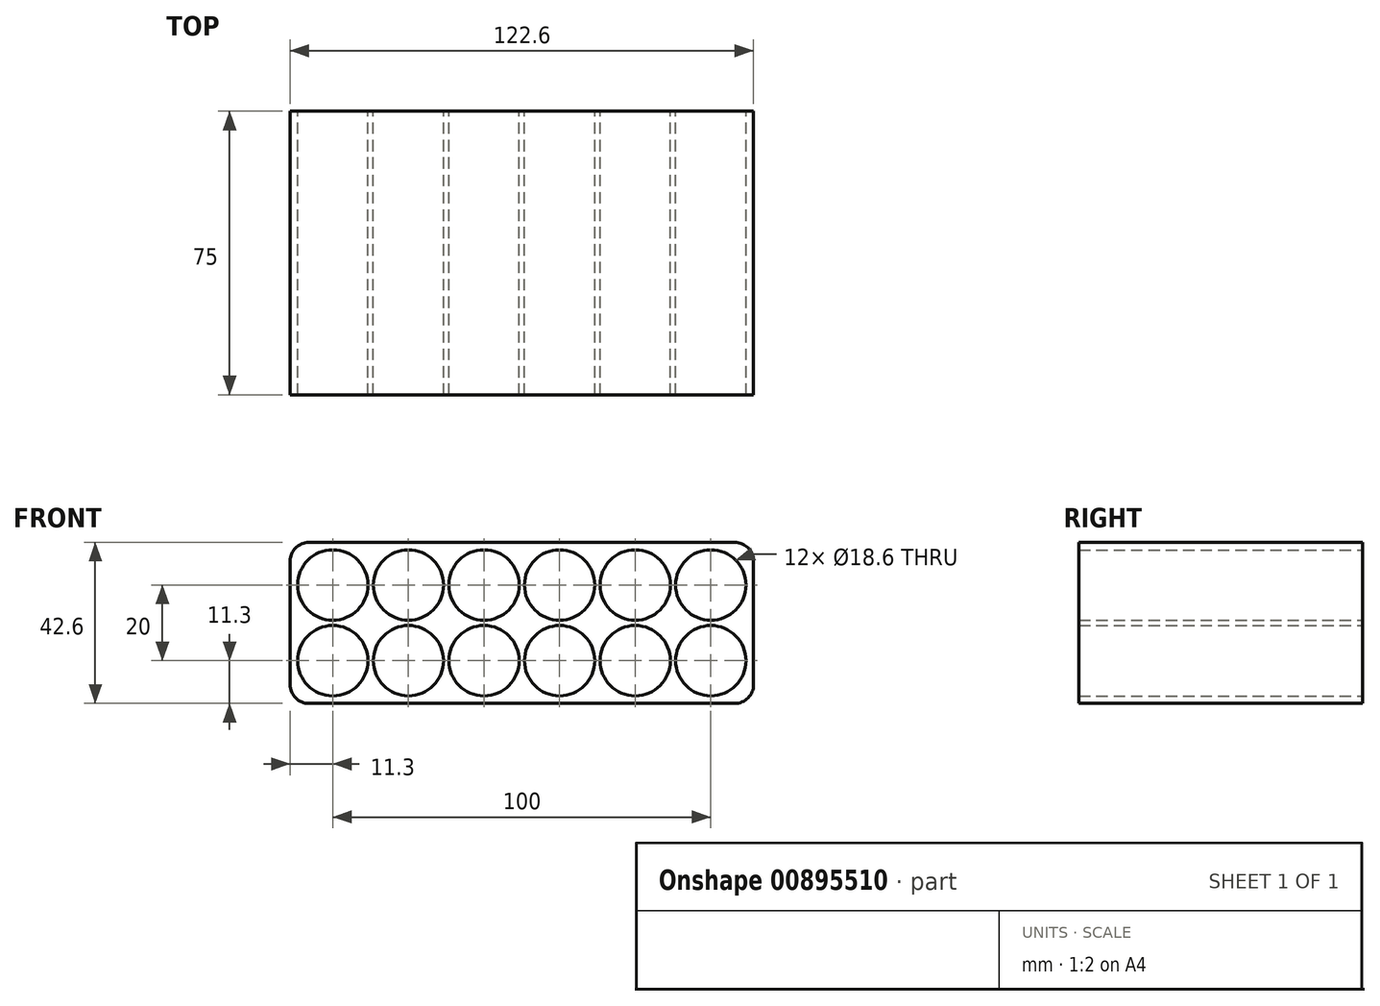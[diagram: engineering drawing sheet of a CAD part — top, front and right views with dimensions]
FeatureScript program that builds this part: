
annotation { "Feature Type Name" : "Feature", "Feature Type Description" : "" }
export const myFeature = defineFeature(function(context is Context, id is Id, definition is map)
    precondition{}
    {
        {
            var Q0;
            Q0=qCreatedBy(makeId("Front.planeOp"),FACE);
            var sketch = newSketch(context, id + "F0", { "sketchPlane" : qUnion([Q0])});
            skCircle(sketch, "E0", {"center": v(0, 0) * mm, "radius": 9.3 * mm});
            skCircle(sketch, "E1.0.1.0", {"center": v(0, 20) * mm, "radius": 9.3 * mm});
            skCircle(sketch, "E1.1.0.0", {"center": v(20, 0) * mm, "radius": 9.3 * mm});
            skCircle(sketch, "E1.1.1.0", {"center": v(20, 20) * mm, "radius": 9.3 * mm});
            skCircle(sketch, "E1.2.0.0", {"center": v(40, 0) * mm, "radius": 9.3 * mm});
            skCircle(sketch, "E1.2.1.0", {"center": v(40, 20) * mm, "radius": 9.3 * mm});
            skCircle(sketch, "E1.3.0.0", {"center": v(60, 0) * mm, "radius": 9.3 * mm});
            skCircle(sketch, "E1.3.1.0", {"center": v(60, 20) * mm, "radius": 9.3 * mm});
            skCircle(sketch, "E1.4.0.0", {"center": v(80, 0) * mm, "radius": 9.3 * mm});
            skCircle(sketch, "E1.4.1.0", {"center": v(80, 20) * mm, "radius": 9.3 * mm});
            skCircle(sketch, "E1.5.0.0", {"center": v(100, 0) * mm, "radius": 9.3 * mm});
            skCircle(sketch, "E1.5.1.0", {"center": v(100, 20) * mm, "radius": 9.3 * mm});
            skLineSegment(sketch, "E1.direction1", {"start": v(0, 0) * mm, "end": v(20, 0) * mm, "construction": true});
            skLineSegment(sketch, "E1.direction2", {"start": v(0, 0) * mm, "end": v(0, 20) * mm, "construction": true});
            skPoint(sketch, "E2", {"position": v(-9.3, 0) * mm});
            skPoint(sketch, "E3", {"position": v(109.3, 20) * mm});
            skPoint(sketch, "E4", {"position": v(100, 29.3) * mm});
            skPoint(sketch, "E5", {"position": v(0, -9.3) * mm});
            skLineSegment(sketch, "E6", {"start": v(0, -9.3) * mm, "end": v(-9.3, -9.3) * mm, "construction": true});
            skLineSegment(sketch, "E7", {"start": v(-9.3, -9.3) * mm, "end": v(-9.3, 29.3) * mm, "construction": true});
            skLineSegment(sketch, "E8", {"start": v(-9.3, 29.3) * mm, "end": v(109.3, 29.3) * mm, "construction": true});
            skLineSegment(sketch, "E9", {"start": v(109.3, 29.3) * mm, "end": v(109.3, -9.3) * mm, "construction": true});
            skLineSegment(sketch, "E10", {"start": v(109.3, -9.3) * mm, "end": v(0, -9.3) * mm, "construction": true});
            skLineSegment(sketch, "E11.0", {"start": v(111.3, -11.3) * mm, "end": v(0, -11.3) * mm});
            skLineSegment(sketch, "E11.1", {"start": v(111.3, 31.3) * mm, "end": v(111.3, -11.3) * mm});
            skLineSegment(sketch, "E11.2", {"start": v(-11.3, 31.3) * mm, "end": v(111.3, 31.3) * mm});
            skLineSegment(sketch, "E11.3", {"start": v(-11.3, -9.3) * mm, "end": v(-11.3, 31.3) * mm});
            skLineSegment(sketch, "E12.0", {"start": v(0, -11.3) * mm, "end": v(-9.3, -11.3) * mm});
            skLineSegment(sketch, "E13", {"start": v(-9.3, -11.3) * mm, "end": v(-11.3, -11.3) * mm});
            skLineSegment(sketch, "E14", {"start": v(-11.3, -11.3) * mm, "end": v(-11.3, -9.3) * mm});
            skSolve(sketch);
        }
        {
            var Q0;
            Q0 = qSketchRegion(id + "F0", true);
            extrude(context, id + "F1", {"entities" : qUnion([Q0]), "depth" : 75 * mm, "offsetDistance" : 25 * mm});
        }
        {
            var Q0;
            Q0=makeQuery(id+"F1.opExtrude","SWEPT_EDGE",EDGE,{"disambiguationData":[OSD([sQuery(id+"F0.wireOp",EDGE,"E11.1"),sQuery(id+"F0.wireOp",EDGE,"E11.2")])]});
            var Q1;
            Q1=makeQuery(id+"F1.opExtrude","SWEPT_EDGE",EDGE,{"disambiguationData":[OSD([sQuery(id+"F0.wireOp",EDGE,"E11.0"),sQuery(id+"F0.wireOp",EDGE,"E11.1")])]});
            var Q2;
            Q2=makeQuery(id+"F1.opExtrude","SWEPT_EDGE",EDGE,{"disambiguationData":[OSD([sQuery(id+"F0.wireOp",EDGE,"E11.2"),sQuery(id+"F0.wireOp",EDGE,"E11.3")])]});
            var Q3;
            Q3=makeQuery(id+"F1.opExtrude","SWEPT_EDGE",EDGE,{"disambiguationData":[OSD([sQuery(id+"F0.wireOp",EDGE,"E13"),sQuery(id+"F0.wireOp",EDGE,"E14")])]});
            fillet(context, id + "F2", {"entities" : qUnion([Q0, Q1, Q2, Q3]), "radius" : 5 * mm, "tangentPropagation" : true, "allowEdgeOverflow" : false});
        }
    });
